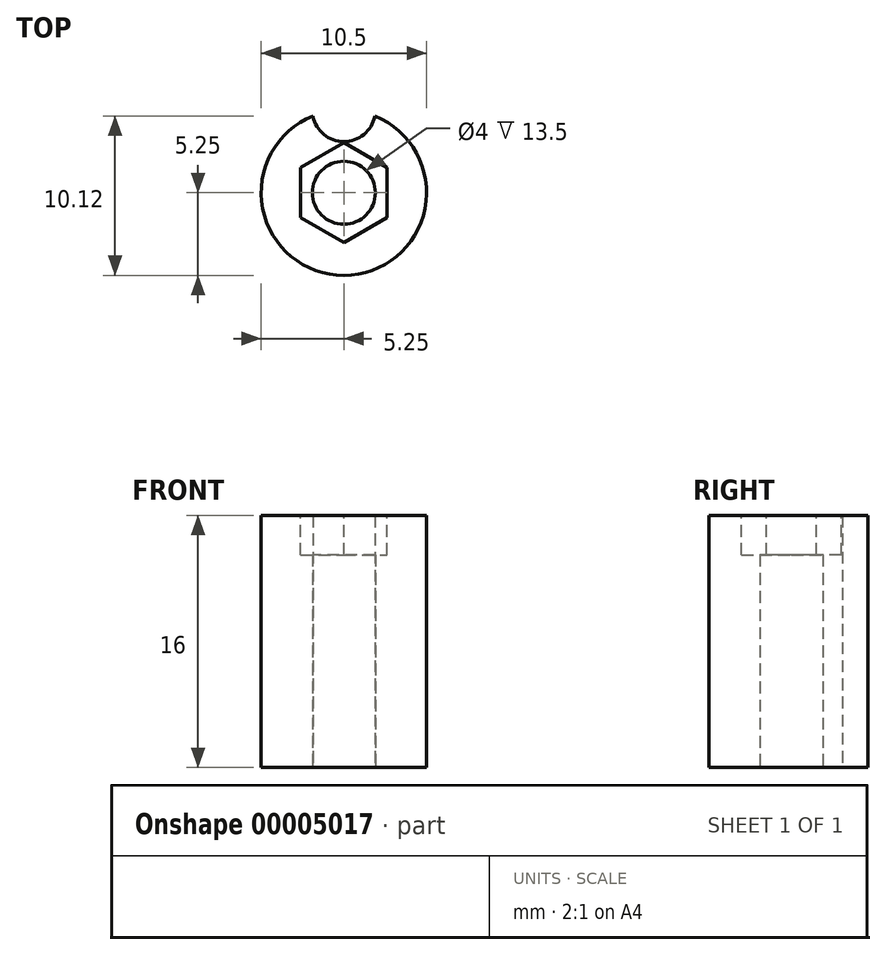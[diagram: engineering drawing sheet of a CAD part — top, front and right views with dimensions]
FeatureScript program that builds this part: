
annotation { "Feature Type Name" : "Feature", "Feature Type Description" : "" }
export const myFeature = defineFeature(function(context is Context, id is Id, definition is map)
    precondition{}
    {
        {
            var Q0;
            Q0=qCreatedBy(makeId("Top.planeOp"),FACE);
            var sketch = newSketch(context, id + "F0", { "sketchPlane" : qUnion([Q0])});
            skArc(sketch, "E0", {"start": v(-1.96, 4.87) * mm, "mid": v(0, -5.25) * mm, "end": v(1.96, 4.87) * mm});
            skCircle(sketch, "E1", {"center": v(0, 0) * mm, "radius": 2 * mm});
            skArc(sketch, "E2", {"start": v(-1.96, 4.87) * mm, "mid": v(0, 3.25) * mm, "end": v(1.96, 4.87) * mm});
            skSolve(sketch);
        }
        {
            var Q0;
            Q0=makeQuery(id+"F0.imprint","IMPRINT",FACE,{"disambiguationData":[TD([[makeQuery(id+"F0.imprint","IMPRINT",EDGE,{"derivedFrom":sQuery(id+"F0.wireOp",EDGE,"E0")}),1.0]])]});
            extrude(context, id + "F1", {"entities" : qUnion([Q0]), "depth" : 16 * mm});
        }
        {
            var Q0;
            Q0=makeQuery(id+"F1.opExtrude","CAP_FACE",FACE,{"disambiguationData":[OSD([sQuery(id+"F0.wireOp",EDGE,"E0")])],"isStart":false});
            var sketch = newSketch(context, id + "F2", { "sketchPlane" : qUnion([Q0])});
            skCircle(sketch, "E3.0.0", {"center": v(0, 0) * mm, "radius": 5.25 * mm, "construction": true});
            skCircle(sketch, "E4.cCircle", {"center": v(0, 0) * mm, "radius": 2.75 * mm, "construction": true});
            skLineSegment(sketch, "E4.0", {"start": v(2.75, 1.59) * mm, "end": v(2.75, -1.59) * mm});
            skLineSegment(sketch, "E4.1", {"start": v(2.75, -1.59) * mm, "end": v(0, -3.18) * mm});
            skLineSegment(sketch, "E4.2", {"start": v(0, -3.18) * mm, "end": v(-2.75, -1.59) * mm});
            skLineSegment(sketch, "E4.3", {"start": v(-2.75, -1.59) * mm, "end": v(-2.75, 1.59) * mm});
            skLineSegment(sketch, "E4.4", {"start": v(-2.75, 1.59) * mm, "end": v(0, 3.18) * mm});
            skLineSegment(sketch, "E4.5", {"start": v(0, 3.18) * mm, "end": v(2.75, 1.59) * mm});
            skPoint(sketch, "E4.0.midPoint", {"position": v(2.75, 0) * mm});
            skSolve(sketch);
        }
        {
            var Q0;
            Q0=makeQuery(id+"F2.imprint","IMPRINT",FACE,{"disambiguationData":[TD([[makeQuery(id+"F2.imprint","IMPRINT",EDGE,{"derivedFrom":sQuery(id+"F2.wireOp",EDGE,"E4.0")}),-1.0]])]});
            extrude(context, id + "F3", {"entities" : qUnion([Q0]), "operationType" : NewBodyOperationType.REMOVE, "oppositeDirection" : true, "depth" : 2.5 * mm});
        }
    });
